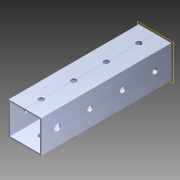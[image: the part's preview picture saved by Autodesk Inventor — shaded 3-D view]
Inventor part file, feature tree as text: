
AUTODESK INVENTOR PART (.ipt)
format: ipt  version: 2014 (Build 180170000, 170)  size: 1,241,088 bytes
history: native  units: in
note: dims shown in document units (in); Inventor stores cm internally (conversion verified against a paired STEP export)
features: extrude x4, sketch x4, pattern_circular x1, other x1, plane x1, imported_body x1
ambient origin geometry x8: Origin, YZ Plane, XZ Plane, XY Plane, X Axis, Y Axis, Z Axis, Center Point
bodies: Body1 (feature_tree)
feature tree (12):
  pattern_circular  "CirPattern2"
  other  "217-3426-STEP1"
  plane  "Work Plane1"
  extrude  "Extrusion1"  Depth=3937.0079in TaperAngle=0.0deg
  extrude  "Extrusion2"  Depth=1.0in TaperAngle=0.0deg
  extrude  "Extrusion3"  Depth=0.3937in TaperAngle=0.0deg
  extrude  "Extrusion4"  [1 undecoded]
  imported_body  "Base1"
  sketch  "Sketch1"  dims[d0=-21.0in d1=3937.0079in d2=0.0in]
  sketch  "Sketch3"  dims[d3=1.0in d4=0.0in d5=16.0in d6=0.0in]
  sketch  "Sketch4"  dims[d7=0.196in d8=0.3937in d9=0.0in]
  sketch  "Sketch5"
note: 1 required parameter value undecoded (feature->parameter linkage not recoverable at this tier; creation-order binding heuristic only, values carry confidence <= 0.55)
